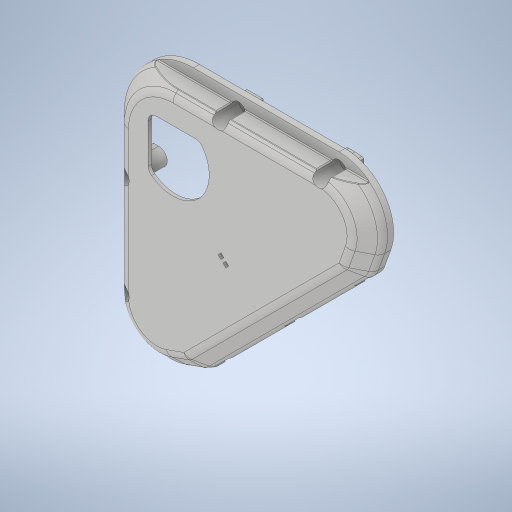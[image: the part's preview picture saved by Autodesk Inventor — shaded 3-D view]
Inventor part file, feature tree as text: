
AUTODESK INVENTOR PART (.ipt)
format: ipt  version: 2023.3 (Build 273359000, 359)  size: 592,384 bytes
history: native  units: in
note: dims shown in document units (in); Inventor stores cm internally (conversion verified against a paired STEP export)
features: sketch x2, extrude x1, hole x1, fillet x1
ambient origin geometry x8: Origin, YZ Plane, XZ Plane, XY Plane, X Axis, Y Axis, Z Axis, Center Point
bodies: Solid2 (feature_tree), Solid1 (feature_tree)
feature tree (5):
  extrude  "Extrusion1"  Depth=0.506in TaperAngle=0.0deg
  hole  "Hole1"  [1 undecoded]
  fillet  "Fillet1"  [1 undecoded]
  sketch  "Sketch1"  dims[d0=0.27in d1=0.506in d2=0.0in]
  sketch  "Sketch2"  dims[d3=0.18in d4=0.75in d5=0.35in d6=0.7in d7=0.563in d8=1.0in d9=0.8108in d10=0.025in]
note: 2 required parameter values undecoded (feature->parameter linkage not recoverable at this tier; creation-order binding heuristic only, values carry confidence <= 0.55)
